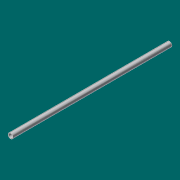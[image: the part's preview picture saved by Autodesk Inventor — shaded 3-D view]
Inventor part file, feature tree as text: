
AUTODESK INVENTOR PART (.ipt)
format: ipt  version: 2017 (Build 210142000, 142)  size: 90,624 bytes
history: native  units: in
note: dims shown in document units (in); Inventor stores cm internally (conversion verified against a paired STEP export)
features: extrude x1, sketch x1
ambient origin geometry x8: Origin, YZ Plane, XZ Plane, XY Plane, X Axis, Y Axis, Z Axis, Center Point
bodies: Solid1 (feature_tree)
feature tree (2):
  extrude  "Extrusion1"  Depth=90.25in
  sketch  "Sketch1"  dims[d0=2.875in d1=2.469in d2=90.25in d3=0.0in]
